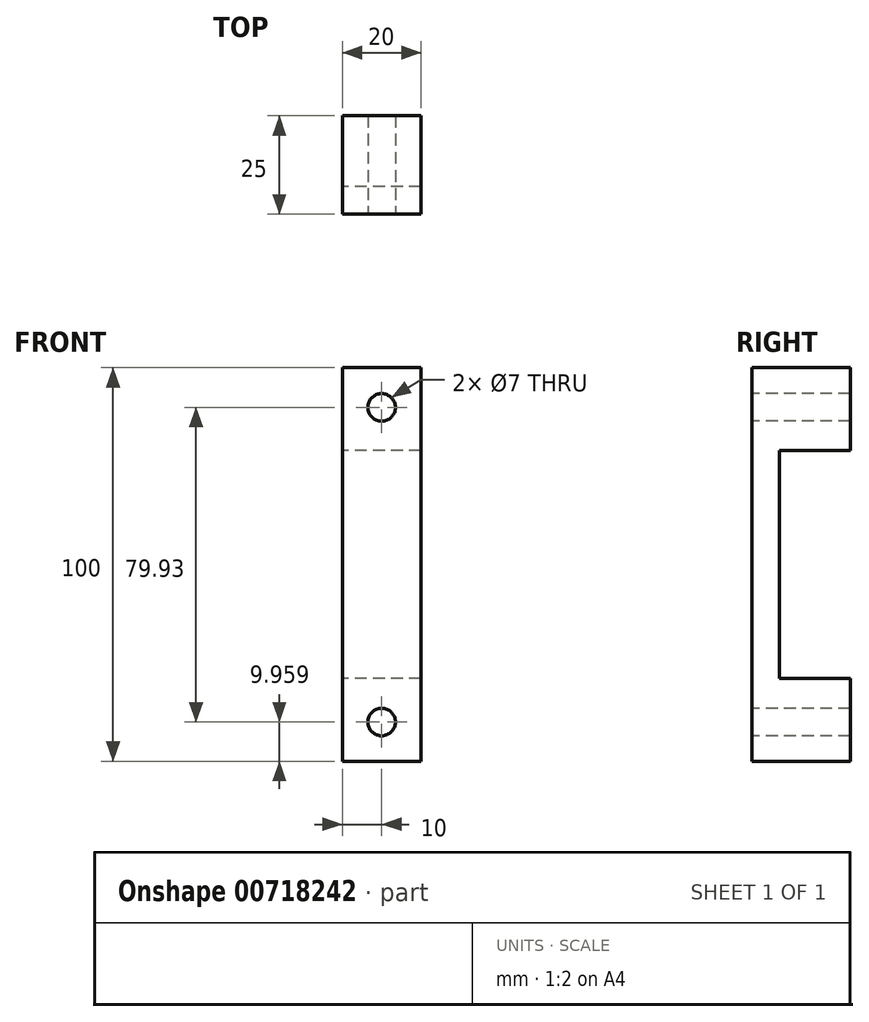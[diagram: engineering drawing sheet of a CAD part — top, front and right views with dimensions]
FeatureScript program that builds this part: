
annotation { "Feature Type Name" : "Feature", "Feature Type Description" : "" }
export const myFeature = defineFeature(function(context is Context, id is Id, definition is map)
    precondition{}
    {
        {
            var Q0;
            Q0=qCreatedBy(makeId("Front.planeOp"),FACE);
            var sketch = newSketch(context, id + "F0", { "sketchPlane" : qUnion([Q0])});
            skLineSegment(sketch, "E0.bottom", {"start": v(0, 0) * mm, "end": v(20, 0) * mm});
            skLineSegment(sketch, "E0.top", {"start": v(0, 100) * mm, "end": v(20, 100) * mm});
            skLineSegment(sketch, "E0.right", {"start": v(20, 0) * mm, "end": v(20, 100) * mm});
            skLineSegment(sketch, "E1", {"start": v(0, 100) * mm, "end": v(0, 0) * mm});
            skSolve(sketch);
        }
        {
            var Q0;
            Q0 = qSketchRegion(id + "F0", true);
            extrude(context, id + "F1", {"entities" : qUnion([Q0]), "depth" : 25 * mm, "offsetDistance" : 25 * mm});
        }
        {
            var Q0;
            Q0=makeQuery(id+"F1.opExtrude","SWEPT_FACE",FACE,{"disambiguationData":[OSD([sQuery(id+"F0.wireOp",EDGE,"E1")])]});
            var sketch = newSketch(context, id + "F2", { "sketchPlane" : qUnion([Q0])});
            skLineSegment(sketch, "E2.bottom", {"start": v(0, 79) * mm, "end": v(18, 79) * mm});
            skLineSegment(sketch, "E2.top", {"start": v(0, 21) * mm, "end": v(18, 21) * mm});
            skLineSegment(sketch, "E2.left", {"start": v(0, 79) * mm, "end": v(0, 21) * mm});
            skLineSegment(sketch, "E2.right", {"start": v(18, 79) * mm, "end": v(18, 21) * mm});
            skSolve(sketch);
        }
        {
            var Q0;
            Q0=makeQuery(id+"F2.imprint","IMPRINT",FACE,{"disambiguationData":[TD([[makeQuery(id+"F2.imprint","IMPRINT",EDGE,{"derivedFrom":sQuery(id+"F2.wireOp",EDGE,"E2.bottom")}),-1.0]])]});
            extrude(context, id + "F3", {"entities" : qUnion([Q0]), "operationType" : NewBodyOperationType.REMOVE, "oppositeDirection" : true, "depth" : 25 * mm, "offsetDistance" : 25 * mm});
        }
        {
            var Q0;
            Q0=makeQuery(id+"F1.opExtrude","CAP_FACE",FACE,{"disambiguationData":[OSD([sQuery(id+"F0.wireOp",EDGE,"E0.bottom"),sQuery(id+"F0.wireOp",EDGE,"E0.top"),sQuery(id+"F0.wireOp",EDGE,"E0.right"),sQuery(id+"F0.wireOp",EDGE,"E1")])],"isStart":false});
            var sketch = newSketch(context, id + "F4", { "sketchPlane" : qUnion([Q0])});
            skCircle(sketch, "E3", {"center": v(10, 89.89) * mm, "radius": 3.5 * mm});
            skCircle(sketch, "E4", {"center": v(10, 9.96) * mm, "radius": 3.5 * mm});
            skSolve(sketch);
        }
        {
            var Q0;
            Q0=makeQuery(id+"F4.imprint","IMPRINT",FACE,{"disambiguationData":[TD([[makeQuery(id+"F4.imprint","IMPRINT",EDGE,{"derivedFrom":sQuery(id+"F4.wireOp",EDGE,"E3")}),1.0]])]});
            var Q1;
            Q1=makeQuery(id+"F4.imprint","IMPRINT",FACE,{"disambiguationData":[TD([[makeQuery(id+"F4.imprint","IMPRINT",EDGE,{"derivedFrom":sQuery(id+"F4.wireOp",EDGE,"E4")}),1.0]])]});
            extrude(context, id + "F5", {"entities" : qUnion([Q0, Q1]), "operationType" : NewBodyOperationType.REMOVE, "oppositeDirection" : true, "depth" : 25 * mm, "offsetDistance" : 25 * mm});
        }
    });
